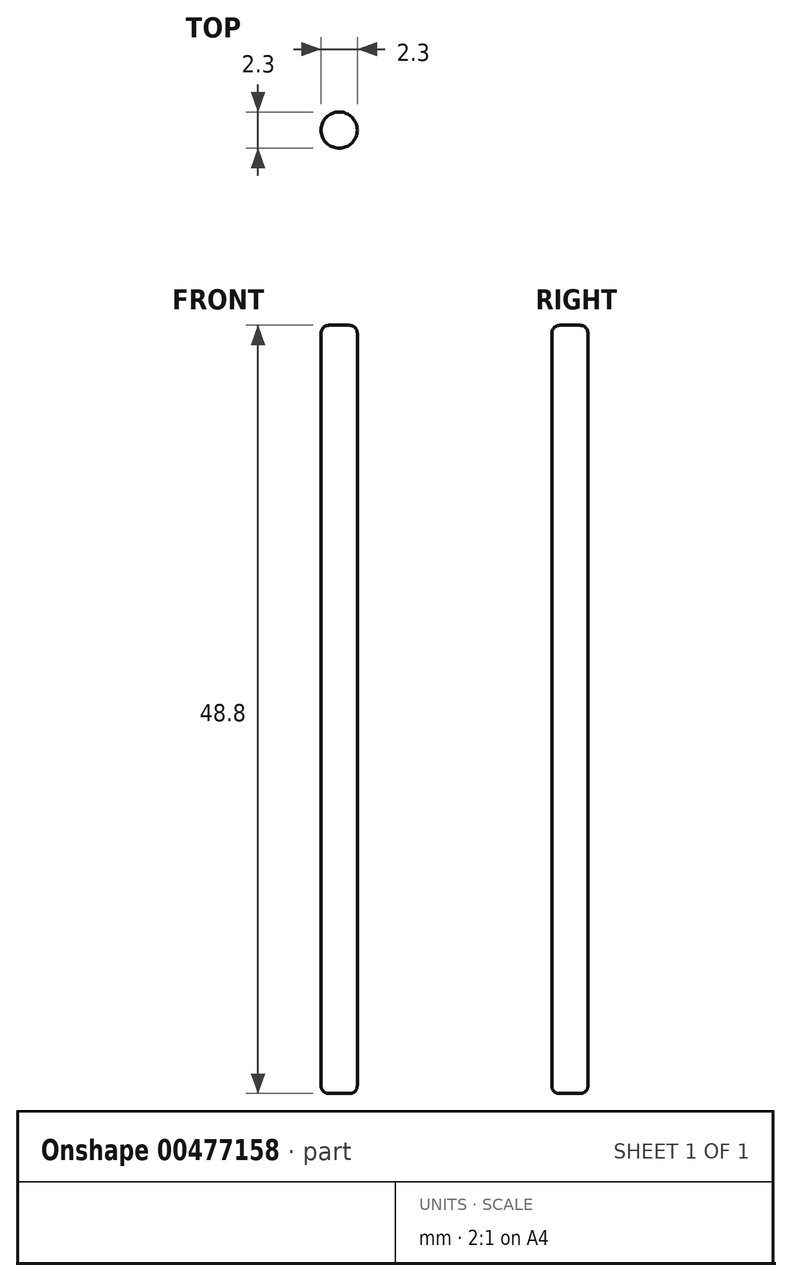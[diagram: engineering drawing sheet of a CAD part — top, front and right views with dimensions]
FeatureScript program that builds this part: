
annotation { "Feature Type Name" : "Feature", "Feature Type Description" : "" }
export const myFeature = defineFeature(function(context is Context, id is Id, definition is map)
    precondition{}
    {
        {
            var Q0;
            Q0=qCreatedBy(makeId("Top.planeOp"),FACE);
            var sketch = newSketch(context, id + "F0", { "sketchPlane" : qUnion([Q0])});
            skCircle(sketch, "E0", {"center": v(0, 0) * mm, "radius": 1.15 * mm});
            skSolve(sketch);
        }
        {
            var Q0;
            Q0=qSketchRegion(id+"F0",true);
            extrude(context, id + "F1", {"entities" : qUnion([Q0]), "depth" : (57 - 8.2) * mm, "offsetDistance" : 25 * mm});
        }
        {
            var Q0;
            Q0=makeQuery(id+"F1.opExtrude","CAP_EDGE",EDGE,{"disambiguationData":[OSD([sQuery(id+"F0.wireOp",EDGE,"E0")])],"isStart":false});
            var Q1;
            Q1=makeQuery(id+"F1.opExtrude","CAP_EDGE",EDGE,{"disambiguationData":[OSD([sQuery(id+"F0.wireOp",EDGE,"E0")])],"isStart":true});
            fillet(context, id + "F2", {"entities" : qUnion([Q0, Q1]), "radius" : 0.5 * mm, "tangentPropagation" : true, "allowEdgeOverflow" : false});
        }
    });
